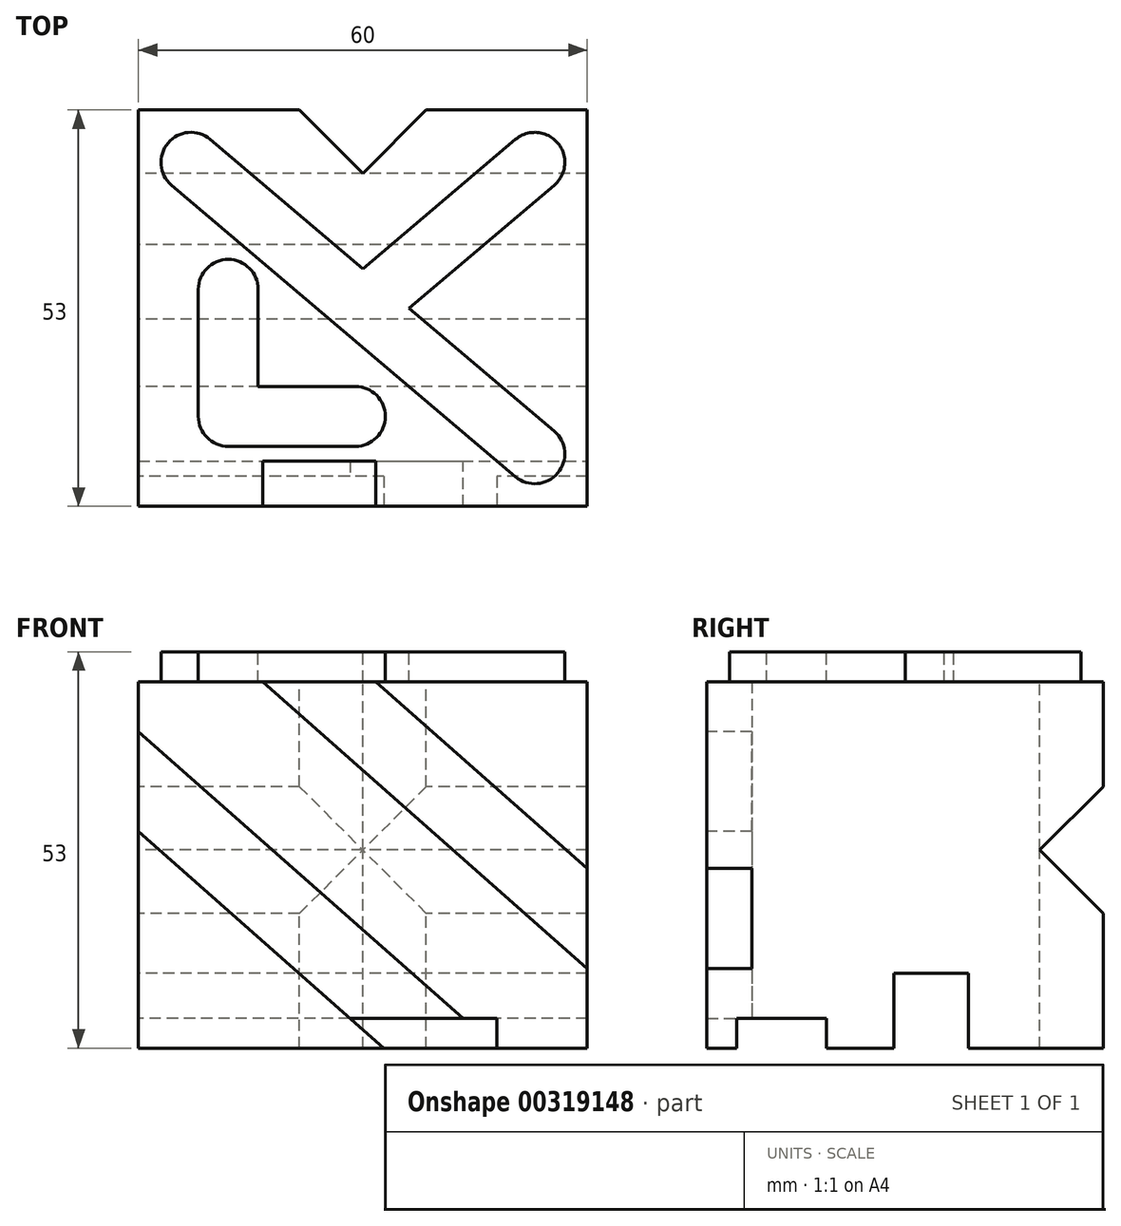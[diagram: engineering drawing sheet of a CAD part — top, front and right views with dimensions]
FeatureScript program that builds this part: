
annotation { "Feature Type Name" : "Feature", "Feature Type Description" : "" }
export const myFeature = defineFeature(function(context is Context, id is Id, definition is map)
    precondition{}
    {
        {
            var Q0;
            Q0=qCreatedBy(makeId("Right.planeOp"),FACE);
            var sketch = newSketch(context, id + "F0", { "sketchPlane" : qUnion([Q0])});
            skLineSegment(sketch, "E0.bottom", {"start": v(53, 0) * mm, "end": v(0, 0) * mm});
            skLineSegment(sketch, "E0.top", {"start": v(53, 53) * mm, "end": v(0, 53) * mm});
            skLineSegment(sketch, "E0.left", {"start": v(53, 0) * mm, "end": v(53, 53) * mm});
            skLineSegment(sketch, "E0.right", {"start": v(0, 0) * mm, "end": v(0, 53) * mm});
            skSolve(sketch);
        }
        {
            var Q0;
            Q0=makeQuery(id+"F0.imprint","IMPRINT",FACE,{"disambiguationData":[TD([[makeQuery(id+"F0.imprint","IMPRINT",EDGE,{"derivedFrom":sQuery(id+"F0.wireOp",EDGE,"E0.bottom")}),-1.0]])]});
            extrude(context, id + "F1", {"entities" : qUnion([Q0]), "depth" : 60 * mm});
        }
        {
            var Q0;
            Q0=makeQuery(id+"F1.opExtrude","SWEPT_FACE",FACE,{"disambiguationData":[OSD([sQuery(id+"F0.wireOp",EDGE,"E0.top")])]});
            var sketch = newSketch(context, id + "F2", { "sketchPlane" : qUnion([Q0])});
            skArc(sketch, "E1.0.startCap", {"start": v(8, 29) * mm, "mid": v(12, 33) * mm, "end": v(16, 29) * mm});
            skArc(sketch, "E1.0.endCap", {"start": v(12, 8) * mm, "mid": v(9.17, 9.17) * mm, "end": v(8, 12) * mm});
            skLineSegment(sketch, "E1.0.left", {"start": v(16, 29) * mm, "end": v(16, 16) * mm});
            skLineSegment(sketch, "E1.0.right", {"start": v(8, 29) * mm, "end": v(8, 12) * mm});
            skArc(sketch, "E1.1.startCap", {"start": v(12, 8) * mm, "mid": v(9.17, 9.17) * mm, "end": v(8, 12) * mm});
            skArc(sketch, "E1.1.endCap", {"start": v(29, 16) * mm, "mid": v(33, 12) * mm, "end": v(29, 8) * mm});
            skLineSegment(sketch, "E1.1.left", {"start": v(16, 16) * mm, "end": v(29, 16) * mm});
            skLineSegment(sketch, "E1.1.right", {"start": v(12, 8) * mm, "end": v(29, 8) * mm});
            skLineSegment(sketch, "E2.bottom", {"start": v(60, 0) * mm, "end": v(53, 0) * mm, "construction": true});
            skLineSegment(sketch, "E2.top", {"start": v(60, 7) * mm, "end": v(53, 7) * mm, "construction": true});
            skLineSegment(sketch, "E2.left", {"start": v(60, 0) * mm, "end": v(60, 7) * mm, "construction": true});
            skLineSegment(sketch, "E2.right", {"start": v(53, 0) * mm, "end": v(53, 7) * mm, "construction": true});
            skLineSegment(sketch, "E3.bottom", {"start": v(0, 53) * mm, "end": v(7, 53) * mm, "construction": true});
            skLineSegment(sketch, "E3.top", {"start": v(0, 46) * mm, "end": v(7, 46) * mm, "construction": true});
            skLineSegment(sketch, "E3.left", {"start": v(0, 53) * mm, "end": v(0, 46) * mm, "construction": true});
            skLineSegment(sketch, "E3.right", {"start": v(7, 53) * mm, "end": v(7, 46) * mm, "construction": true});
            skArc(sketch, "E4.0.startCap", {"start": v(4.41, 42.95) * mm, "mid": v(3.95, 48.59) * mm, "end": v(9.59, 49.05) * mm});
            skArc(sketch, "E4.0.endCap", {"start": v(55.59, 10.05) * mm, "mid": v(56.05, 4.41) * mm, "end": v(50.41, 3.95) * mm});
            skLineSegment(sketch, "E4.0.left", {"start": v(9.59, 49.05) * mm, "end": v(30, 31.74) * mm});
            skLineSegment(sketch, "E4.0.right", {"start": v(4.41, 42.95) * mm, "end": v(50.41, 3.95) * mm});
            skPoint(sketch, "E5", {"position": v(30, 26.5) * mm});
            skArc(sketch, "E6.0.endCap", {"start": v(50.41, 49.05) * mm, "mid": v(56.05, 48.59) * mm, "end": v(55.59, 42.95) * mm});
            skLineSegment(sketch, "E6.0.left", {"start": v(30, 31.74) * mm, "end": v(50.41, 49.05) * mm});
            skLineSegment(sketch, "E7.trimOffspring", {"start": v(36.19, 26.5) * mm, "end": v(55.59, 10.05) * mm});
            skLineSegment(sketch, "E8", {"start": v(21.52, 53) * mm, "end": v(30, 44.52) * mm});
            skPoint(sketch, "E8.endSnap0", {"position": v(30, 53) * mm});
            skLineSegment(sketch, "E9", {"start": v(30, 79.74) * mm, "end": v(30, 95.62) * mm, "construction": true});
            skLineSegment(sketch, "E10.MirrorCS", {"start": v(38.48, 53) * mm, "end": v(30, 44.52) * mm});
            skPoint(sketch, "E11", {"position": v(0, 23.4) * mm});
            skPoint(sketch, "E12", {"position": v(60, 20.14) * mm});
            skLineSegment(sketch, "E13.trimOffspring", {"start": v(36.19, 26.5) * mm, "end": v(55.59, 42.95) * mm});
            skSolve(sketch);
        }
        {
            var Q0;
            {var subQ5=sQuery(id+"F2.wireOp",EDGE,"E4.0.startCap");Q0=makeQuery(id+"F2.imprint","IMPRINT",FACE,{"disambiguationData":[TD([[makeQuery(id+"F2.imprint","IMPRINT",EDGE,{"derivedFrom":subQ5}),-1.0]])]});}
            var Q1;
            {var subQ7=sQuery(id+"F2.wireOp",EDGE,"E4.0.endCap");Q1=makeQuery(id+"F2.imprint","IMPRINT",FACE,{"disambiguationData":[TD([[makeQuery(id+"F2.imprint","IMPRINT",EDGE,{"derivedFrom":subQ7}),-1.0]])]});}
            var Q2;
            {var subQ4=sQuery(id+"F2.wireOp",EDGE,"E6.0.endCap");Q2=makeQuery(id+"F2.imprint","IMPRINT",FACE,{"disambiguationData":[TD([[makeQuery(id+"F2.imprint","IMPRINT",EDGE,{"derivedFrom":subQ4}),-1.0]])]});}
            var Q3;
            Q3=makeQuery(id+"F2.imprint","IMPRINT",FACE,{"disambiguationData":[TD([[makeQuery(id+"F2.imprint","IMPRINT",EDGE,{"derivedFrom":sQuery(id+"F2.wireOp",EDGE,"E1.0.startCap")}),-1.0]])]});
            extrude(context, id + "F3", {"entities" : qUnion([Q0, Q1, Q2, Q3]), "operationType" : NewBodyOperationType.REMOVE, "oppositeDirection" : true, "depth" : 4 * mm});
        }
        {
            var Q0;
            {var subQ0=sQuery(id+"F2.wireOp",EDGE,"E8");Q0=makeQuery(id+"F2.imprint","IMPRINT",FACE,{"disambiguationData":[TD([[makeQuery(id+"F2.imprint","IMPRINT",EDGE,{"derivedFrom":subQ0}),1.0]])]});}
            var Q1;
            Q1=makeQuery(id+"F1.opExtrude","CAP_VERTEX",VERTEX,{"disambiguationData":[OSD([sQuery(id+"F0.wireOp",EDGE,"E0.bottom"),sQuery(id+"F0.wireOp",EDGE,"E0.left")])],"isStart":false});
            extrude(context, id + "F4", {"entities" : qUnion([Q0]), "operationType" : NewBodyOperationType.REMOVE, "endBound" : BoundingType.UP_TO_VERTEX, "oppositeDirection" : true, "endBoundEntityVertex" : qUnion([Q1]), "depth" : 25 * mm});
        }
        {
            var Q0;
            Q0=makeQuery(id+"F1.opExtrude","SWEPT_FACE",FACE,{"disambiguationData":[OSD([sQuery(id+"F0.wireOp",EDGE,"E0.right")])]});
            var sketch = newSketch(context, id + "F5", { "sketchPlane" : qUnion([Q0])});
            skLineSegment(sketch, "E14.bottom", {"start": v(0, 53) * mm, "end": v(60, 53) * mm});
            skLineSegment(sketch, "E14.top", {"start": v(0, 0) * mm, "end": v(60, 0) * mm});
            skLineSegment(sketch, "E14.left", {"start": v(0, 53) * mm, "end": v(0, 0) * mm});
            skLineSegment(sketch, "E14.right", {"start": v(60, 53) * mm, "end": v(60, 0) * mm});
            skLineSegment(sketch, "E15", {"start": v(0, 53) * mm, "end": v(60, 0) * mm, "construction": true});
            skLineSegment(sketch, "E16", {"start": v(0, 42.33) * mm, "end": v(47.92, 0) * mm});
            skLineSegment(sketch, "E17", {"start": v(0, 28.98) * mm, "end": v(32.81, 0) * mm});
            skLineSegment(sketch, "E18", {"start": v(27.19, 53) * mm, "end": v(60, 24.02) * mm});
            skLineSegment(sketch, "E19", {"start": v(12.08, 53) * mm, "end": v(60, 10.67) * mm});
            skSolve(sketch);
        }
        {
            var Q0;
            {var subQ0=sQuery(id+"F5.wireOp",EDGE,"E18");Q0=makeQuery(id+"F5.imprint","IMPRINT",FACE,{"disambiguationData":[TD([[makeQuery(id+"F5.imprint","IMPRINT",EDGE,{"derivedFrom":subQ0}),-1.0]])]});}
            var Q1;
            {var subQ0=sQuery(id+"F5.wireOp",EDGE,"E16");Q1=makeQuery(id+"F5.imprint","IMPRINT",FACE,{"disambiguationData":[TD([[makeQuery(id+"F5.imprint","IMPRINT",EDGE,{"derivedFrom":subQ0}),-1.0]])]});}
            extrude(context, id + "F6", {"entities" : qUnion([Q0, Q1]), "operationType" : NewBodyOperationType.REMOVE, "oppositeDirection" : true, "depth" : 6 * mm});
        }
        {
            var Q0;
            Q0=makeQuery(id+"F1.opExtrude","CAP_FACE",FACE,{"disambiguationData":[OSD([sQuery(id+"F0.wireOp",EDGE,"E0.bottom"),sQuery(id+"F0.wireOp",EDGE,"E0.top"),sQuery(id+"F0.wireOp",EDGE,"E0.left"),sQuery(id+"F0.wireOp",EDGE,"E0.right")])],"isStart":true});
            var sketch = newSketch(context, id + "F7", { "sketchPlane" : qUnion([Q0])});
            skLineSegment(sketch, "E20", {"start": v(-53, 34.98) * mm, "end": v(-44.52, 26.5) * mm});
            skPoint(sketch, "E20.endSnap0", {"position": v(-53, 26.5) * mm});
            skLineSegment(sketch, "E21", {"start": v(-76.86, 26.5) * mm, "end": v(-99.72, 26.5) * mm, "construction": true});
            skLineSegment(sketch, "E22.MirrorCS", {"start": v(-53, 18.02) * mm, "end": v(-44.52, 26.5) * mm});
            skLineSegment(sketch, "E23", {"start": v(-53, 18.02) * mm, "end": v(-53, 34.98) * mm});
            skSolve(sketch);
        }
        {
            var Q0;
            Q0=makeQuery(id+"F7.imprint","IMPRINT",FACE,{"disambiguationData":[TD([[makeQuery(id+"F7.imprint","IMPRINT",EDGE,{"derivedFrom":sQuery(id+"F7.wireOp",EDGE,"E20")}),-1.0]])]});
            var Q1;
            Q1=makeQuery(id+"F1.opExtrude","CAP_VERTEX",VERTEX,{"disambiguationData":[OSD([sQuery(id+"F0.wireOp",EDGE,"E0.bottom"),sQuery(id+"F0.wireOp",EDGE,"E0.left")])],"isStart":false});
            extrude(context, id + "F8", {"entities" : qUnion([Q0]), "operationType" : NewBodyOperationType.REMOVE, "endBound" : BoundingType.UP_TO_VERTEX, "oppositeDirection" : true, "endBoundEntityVertex" : qUnion([Q1]), "depth" : 25 * mm});
        }
        {
            var Q0;
            Q0=makeQuery(id+"F1.opExtrude","SWEPT_FACE",FACE,{"disambiguationData":[OSD([sQuery(id+"F0.wireOp",EDGE,"E0.bottom")])]});
            var sketch = newSketch(context, id + "F9", { "sketchPlane" : qUnion([Q0])});
            skLineSegment(sketch, "E24.bottom", {"start": v(60, -53) * mm, "end": v(0, -53) * mm});
            skLineSegment(sketch, "E24.top", {"start": v(60, 0) * mm, "end": v(0, 0) * mm});
            skLineSegment(sketch, "E24.left", {"start": v(60, -53) * mm, "end": v(60, 0) * mm});
            skLineSegment(sketch, "E24.right", {"start": v(0, -53) * mm, "end": v(0, 0) * mm});
            skLineSegment(sketch, "E25.top", {"start": v(60, -45) * mm, "end": v(0, -45) * mm});
            skLineSegment(sketch, "E25.left", {"start": v(60, -53) * mm, "end": v(60, -45) * mm});
            skLineSegment(sketch, "E25.right", {"start": v(0, -53) * mm, "end": v(0, -45) * mm});
            skLineSegment(sketch, "E26.top", {"start": v(60, -35) * mm, "end": v(0, -35) * mm});
            skLineSegment(sketch, "E26.left", {"start": v(60, -45) * mm, "end": v(60, -35) * mm});
            skLineSegment(sketch, "E26.right", {"start": v(0, -45) * mm, "end": v(0, -35) * mm});
            skLineSegment(sketch, "E27.top", {"start": v(60, -25) * mm, "end": v(0, -25) * mm});
            skLineSegment(sketch, "E27.left", {"start": v(60, -35) * mm, "end": v(60, -25) * mm});
            skLineSegment(sketch, "E27.right", {"start": v(0, -35) * mm, "end": v(0, -25) * mm});
            skLineSegment(sketch, "E28.top", {"start": v(60, -16) * mm, "end": v(0, -16) * mm});
            skLineSegment(sketch, "E28.left", {"start": v(60, -25) * mm, "end": v(60, -16) * mm});
            skLineSegment(sketch, "E28.right", {"start": v(0, -25) * mm, "end": v(0, -16) * mm});
            skLineSegment(sketch, "E29.top", {"start": v(60, -4) * mm, "end": v(0, -4) * mm});
            skLineSegment(sketch, "E29.left", {"start": v(60, -16) * mm, "end": v(60, -4) * mm});
            skLineSegment(sketch, "E29.right", {"start": v(0, -16) * mm, "end": v(0, -4) * mm});
            skSolve(sketch);
        }
        {
            var Q0;
            Q0=makeQuery(id+"F9.imprint","IMPRINT",FACE,{"disambiguationData":[TD([[makeQuery(id+"F9.imprint","IMPRINT",EDGE,{"derivedFrom":sQuery(id+"F9.wireOp",EDGE,"E28.top")}),-1.0]])]});
            var Q1;
            {var subQ1=sQuery(id+"F9.wireOp",EDGE,"E25.left");Q1=makeQuery(id+"F9.imprint","IMPRINT",FACE,{"disambiguationData":[TD([[makeQuery(id+"F9.imprint","IMPRINT",EDGE,{"derivedFrom":subQ1}),1.0]])]});}
            extrude(context, id + "F10", {"entities" : qUnion([Q0, Q1]), "operationType" : NewBodyOperationType.REMOVE, "oppositeDirection" : true, "depth" : 4 * mm});
        }
        {
            var Q0;
            Q0=makeQuery(id+"F9.imprint","IMPRINT",FACE,{"disambiguationData":[TD([[makeQuery(id+"F9.imprint","IMPRINT",EDGE,{"derivedFrom":sQuery(id+"F9.wireOp",EDGE,"E26.top")}),-1.0]])]});
            extrude(context, id + "F11", {"entities" : qUnion([Q0]), "operationType" : NewBodyOperationType.REMOVE, "oppositeDirection" : true, "depth" : 10 * mm});
        }
        {
            var Q0;
            Q0=makeQuery(id+"F10.boolean.opBoolean","COPY",FACE,{"derivedFrom":makeQuery(id+"F10.opExtrude","SWEPT_FACE",FACE,{"disambiguationData":[OSD([sQuery(id+"F5.wireOp",EDGE,"E14.top"),sQuery(id+"F5.wireOp",EDGE,"E16")])]})});
            extrude(context, id + "F12", {"entities" : qUnion([Q0]), "operationType" : NewBodyOperationType.REMOVE, "oppositeDirection" : true, "depth" : 25 * mm});
        }
    });
